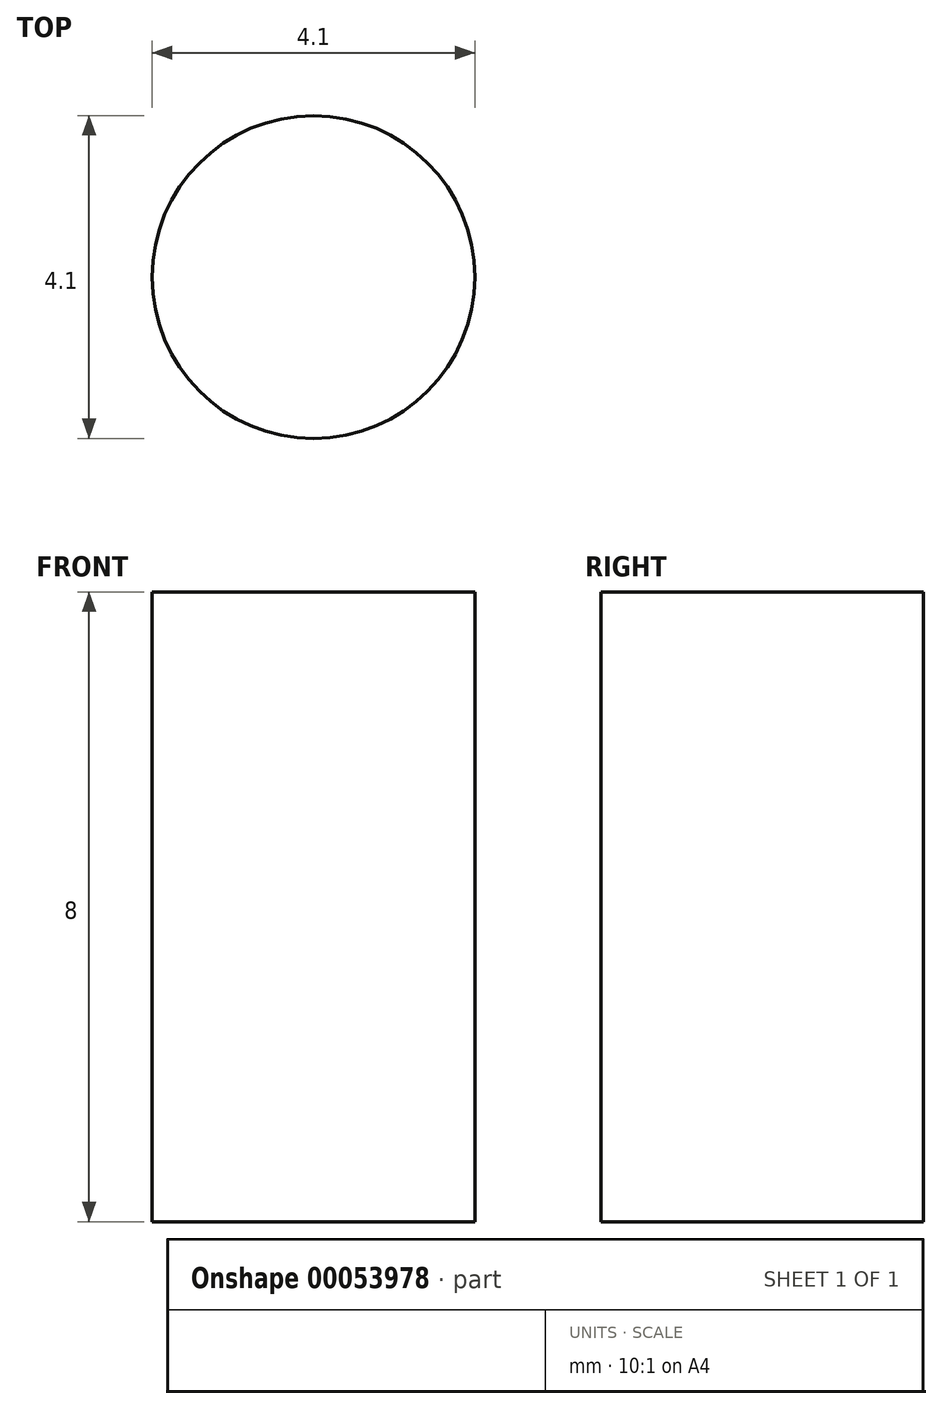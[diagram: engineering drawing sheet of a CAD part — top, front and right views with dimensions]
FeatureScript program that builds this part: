
annotation { "Feature Type Name" : "Feature", "Feature Type Description" : "" }
export const myFeature = defineFeature(function(context is Context, id is Id, definition is map)
    precondition{}
    {
        {
            var Q0;
            Q0=qCreatedBy(makeId("Top.planeOp"),FACE);
            var sketch = newSketch(context, id + "F0", { "sketchPlane" : qUnion([Q0])});
            skCircle(sketch, "E0", {"center": v(0, 0) * mm, "radius": 2.05 * mm});
            skSolve(sketch);
        }
        {
            var Q0;
            Q0=sQuery(id+"F0.wireOp",EDGE,"E0");
            extrude(context, id + "F1", {"bodyType" : ToolBodyType.SURFACE, "surfaceEntities" : qUnion([Q0]), "depth" : 8 * mm});
        }
    });
